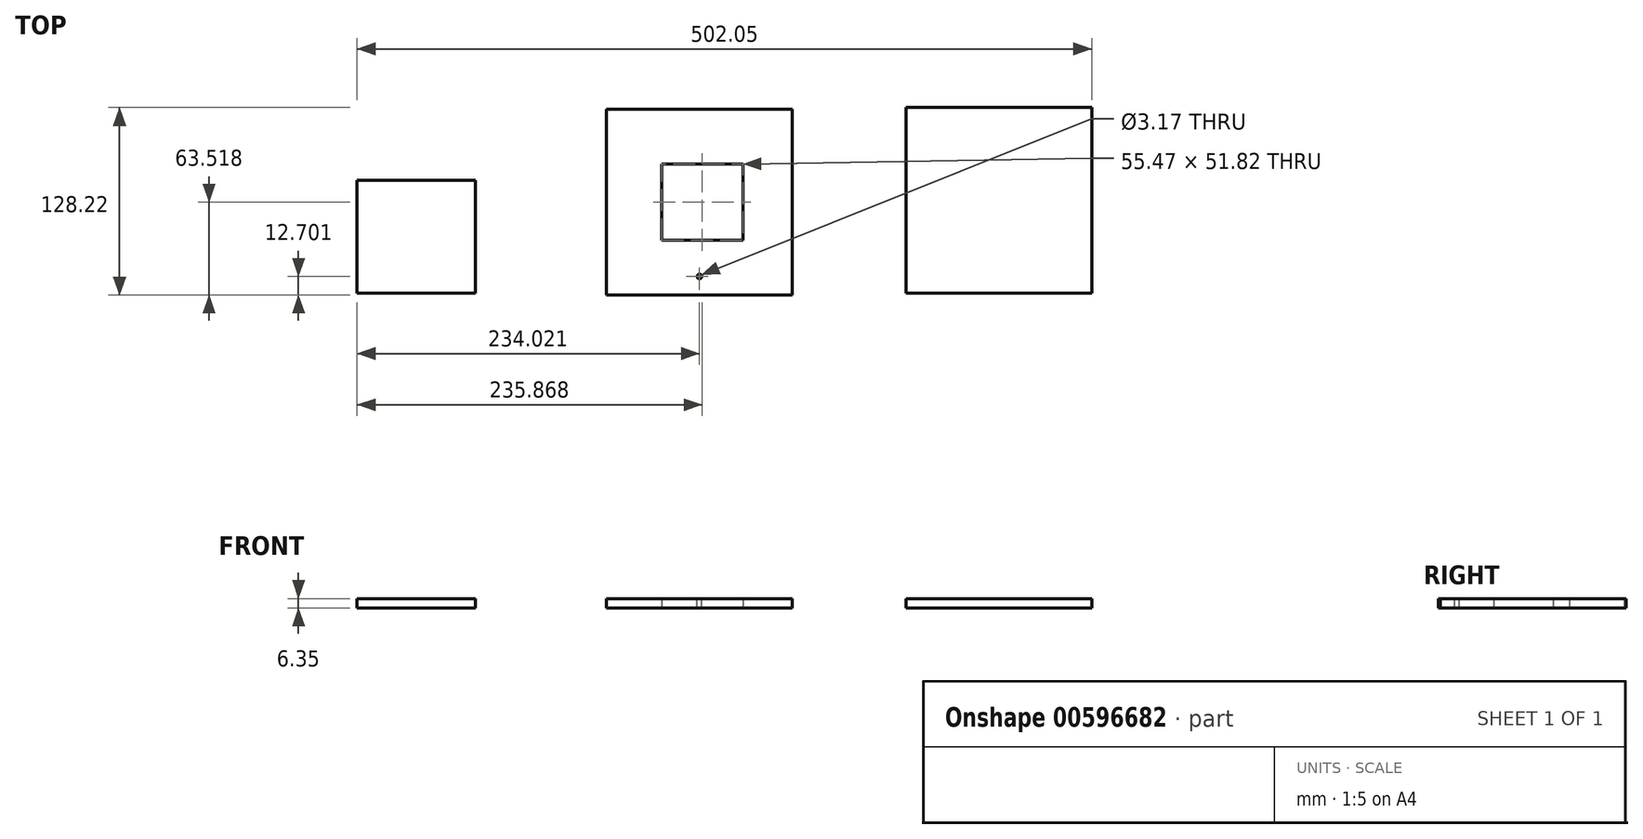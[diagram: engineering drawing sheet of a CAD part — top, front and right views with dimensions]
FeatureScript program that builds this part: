
annotation { "Feature Type Name" : "Feature", "Feature Type Description" : "" }
export const myFeature = defineFeature(function(context is Context, id is Id, definition is map)
    precondition{}
    {
        {
            var Q0;
            Q0=qCreatedBy(makeId("Top.planeOp"),FACE);
            var sketch = newSketch(context, id + "F0", { "sketchPlane" : qUnion([Q0])});
            skLineSegment(sketch, "E0.bottom", {"start": v(0, 0) * mm, "end": v(127, 0) * mm});
            skLineSegment(sketch, "E0.top", {"start": v(0, 127) * mm, "end": v(127, 127) * mm});
            skLineSegment(sketch, "E0.left", {"start": v(0, 0) * mm, "end": v(0, 127) * mm});
            skLineSegment(sketch, "E0.right", {"start": v(127, 0) * mm, "end": v(127, 127) * mm});
            skLineSegment(sketch, "E1.bottom", {"start": v(-204.53, -1.22) * mm, "end": v(-77.53, -1.22) * mm});
            skLineSegment(sketch, "E1.top", {"start": v(-204.53, 125.78) * mm, "end": v(-77.53, 125.78) * mm});
            skLineSegment(sketch, "E1.left", {"start": v(-204.53, -1.22) * mm, "end": v(-204.53, 125.78) * mm});
            skLineSegment(sketch, "E1.right", {"start": v(-77.53, -1.22) * mm, "end": v(-77.53, 125.78) * mm});
            skLineSegment(sketch, "E2", {"start": v(-166.92, 88.2) * mm, "end": v(-111.45, 88.2) * mm});
            skLineSegment(sketch, "E3", {"start": v(-111.45, 88.2) * mm, "end": v(-111.45, 62.28) * mm});
            skLineSegment(sketch, "E4", {"start": v(-111.45, 36.4) * mm, "end": v(-111.45, 62.28) * mm});
            skLineSegment(sketch, "E5", {"start": v(-111.45, 36.4) * mm, "end": v(-141.03, 36.4) * mm});
            skLineSegment(sketch, "E6", {"start": v(-141.03, 36.4) * mm, "end": v(-166.92, 36.4) * mm});
            skLineSegment(sketch, "E7", {"start": v(-166.92, 36.4) * mm, "end": v(-166.92, 62.28) * mm});
            skLineSegment(sketch, "E8", {"start": v(-166.92, 88.2) * mm, "end": v(-166.92, 88.2) * mm});
            skLineSegment(sketch, "E9", {"start": v(-166.92, 88.2) * mm, "end": v(-166.92, 62.28) * mm});
            skPoint(sketch, "E10.start.orphan", {"position": v(-141.03, 62.28) * mm});
            skLineSegment(sketch, "E11", {"start": v(-141.03, -1.22) * mm, "end": v(-141.03, 11.48) * mm});
            skSolve(sketch);
        }
        {
            var Q0;
            Q0 = qSketchRegion(id + "F0", true);
            extrude(context, id + "F1", {"entities" : qUnion([Q0]), "depth" : 6.35 * mm, "offsetDistance" : 25.4 * mm});
        }
        {
            var Q0;
            Q0=qCreatedBy(makeId("Top.planeOp"),FACE);
            var sketch = newSketch(context, id + "F2", { "sketchPlane" : qUnion([Q0])});
            skLineSegment(sketch, "E12.bottom", {"start": v(-294.2, 0) * mm, "end": v(-375.05, 0) * mm});
            skLineSegment(sketch, "E12.top", {"start": v(-294.2, 77.18) * mm, "end": v(-375.05, 77.18) * mm});
            skLineSegment(sketch, "E12.left", {"start": v(-294.2, 0) * mm, "end": v(-294.2, 77.18) * mm});
            skLineSegment(sketch, "E12.right", {"start": v(-375.05, 0) * mm, "end": v(-375.05, 77.18) * mm});
            skSolve(sketch);
        }
        {
            var Q0;
            Q0=makeQuery(id+"F2.imprint","IMPRINT",FACE,{"disambiguationData":[TD([[makeQuery(id+"F2.imprint","IMPRINT",EDGE,{"derivedFrom":sQuery(id+"F2.wireOp",EDGE,"E12.bottom")}),-1.0]])]});
            extrude(context, id + "F3", {"entities" : qUnion([Q0]), "depth" : 6.35 * mm, "offsetDistance" : 25.4 * mm});
        }
        {
            var Q0;
            Q0=makeQuery(id+"F1.opExtrude","CAP_FACE",FACE,{"disambiguationData":[OSD([sQuery(id+"F0.wireOp",EDGE,"E1.bottom"),sQuery(id+"F0.wireOp",EDGE,"E1.top"),sQuery(id+"F0.wireOp",EDGE,"E1.left"),sQuery(id+"F0.wireOp",EDGE,"E1.right"),sQuery(id+"F0.wireOp",EDGE,"E2"),sQuery(id+"F0.wireOp",EDGE,"E3"),sQuery(id+"F0.wireOp",EDGE,"E4"),sQuery(id+"F0.wireOp",EDGE,"E5"),sQuery(id+"F0.wireOp",EDGE,"E6"),sQuery(id+"F0.wireOp",EDGE,"E7"),sQuery(id+"F0.wireOp",EDGE,"E9")])],"isStart":false});
            var sketch = newSketch(context, id + "F4", { "sketchPlane" : qUnion([Q0])});
            skLineSegment(sketch, "E13", {"start": v(-141.03, -1.22) * mm, "end": v(-141.03, 11.48) * mm});
            skSolve(sketch);
        }
        {
            var Q0;
            Q0=sQuery(id+"F4.wireOp",VERTEX,"E13.end");
            var Q1;
            Q1=makeQuery(id+"F1.opExtrude","SWEPT_BODY",BODY,{"disambiguationData":[OSD([sQuery(id+"F0.wireOp",EDGE,"E1.bottom"),sQuery(id+"F0.wireOp",EDGE,"E1.top"),sQuery(id+"F0.wireOp",EDGE,"E1.left"),sQuery(id+"F0.wireOp",EDGE,"E1.right"),sQuery(id+"F0.wireOp",EDGE,"E2"),sQuery(id+"F0.wireOp",EDGE,"E3"),sQuery(id+"F0.wireOp",EDGE,"E4"),sQuery(id+"F0.wireOp",EDGE,"E5"),sQuery(id+"F0.wireOp",EDGE,"E6"),sQuery(id+"F0.wireOp",EDGE,"E7"),sQuery(id+"F0.wireOp",EDGE,"E9")])]});
            hole(context, id + "F5", {"style" : HoleStyle.SIMPLE, "endStyle" : HoleEndStyle.BLIND, "holeDiameter" : 3.17 * mm, "majorDiameter" : 6.35 * mm, "holeDepth" : 63.5 * mm, "isTappedThrough" : true, "tappedDepth" : 12.7 * mm, "tapClearance" : 3, "locations" : qUnion([Q0]), "scope" : qUnion([Q1])});
        }
    });
